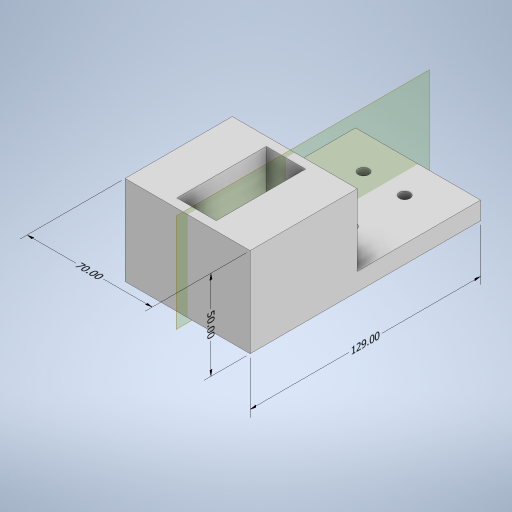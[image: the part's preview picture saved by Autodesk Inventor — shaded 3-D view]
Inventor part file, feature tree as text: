
AUTODESK INVENTOR PART (.ipt)
format: ipt  version: 2023 (Build 270158000, 158)  size: 287,744 bytes
history: native  units: mm
features: other x5, extrude x4, sketch x4, plane x1
ambient origin geometry x8: Origin, YZ Plane, XZ Plane, XY Plane, X Axis, Y Axis, Z Axis, Center Point
bodies: Body1 (feature_tree)
feature tree (14):
  other  "Sólido1"
  other  "Anotaciones"
  extrude  "Extrusión1"  Depth=10.0mm TaperAngle=0.0deg
  extrude  "Extrusión2"  Depth=50.0mm TaperAngle=0.0deg
  extrude  "Extrusión3"  Depth=50.0mm
  plane  "Plano de trabajo1"
  extrude  "Extrusión4"  Depth=70.0mm
  sketch  "Boceto1"  dims[d0=20.0mm d1=20.0mm d2=30.0mm d3=30.0mm d4=20.0mm d5=35.0mm d6=35.0mm d7=69.0mm d8=10.0mm d9=0.0mm]
  sketch  "Boceto2"  dims[d10=60.0mm d11=50.0mm d12=0.0mm]
  sketch  "Boceto3"  dims[d13=22.0mm d14=50.0mm]
  sketch  "Boceto4"  dims[d15=43.0mm d16=0.0mm d17=30.0mm d18=15.0mm d19=0.0mm d20=7.347286mm d21=2.970698mm d22=50.0mm d23=4.430856mm d24=4.754925mm d25=129.0mm d26=4.790648mm d27=5.675476mm d28=70.0mm]
  other  "Cota lineal 1"
  other  "Cota lineal 2"
  other  "Cota lineal 3"
